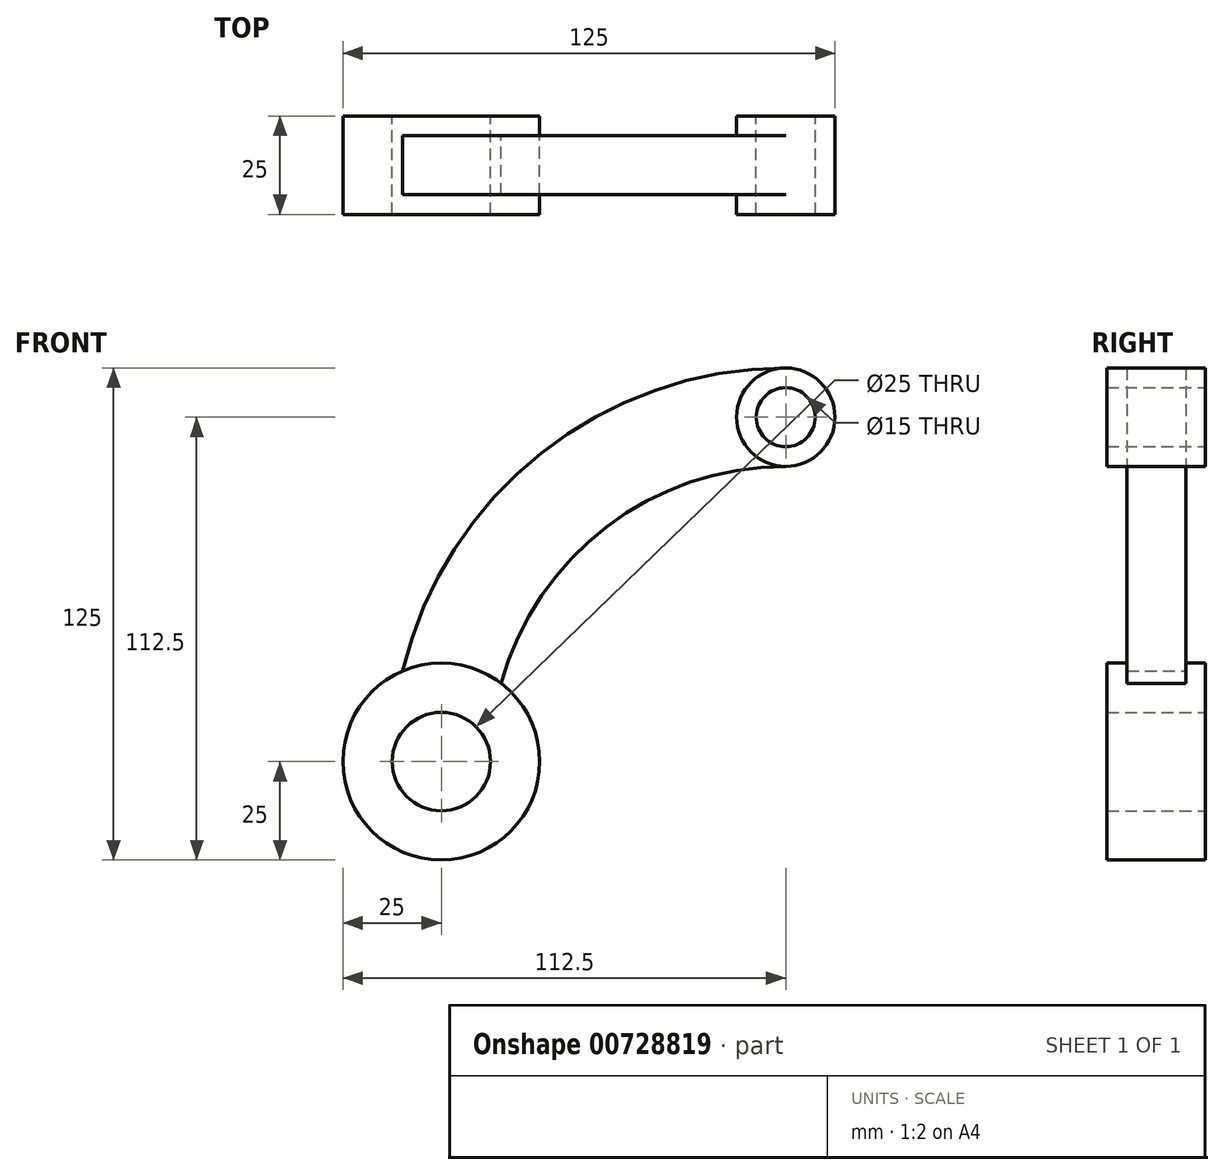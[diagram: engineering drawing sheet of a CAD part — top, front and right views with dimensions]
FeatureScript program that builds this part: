
annotation { "Feature Type Name" : "Feature", "Feature Type Description" : "" }
export const myFeature = defineFeature(function(context is Context, id is Id, definition is map)
    precondition{}
    {
        {
            var Q0;
            Q0=qCreatedBy(makeId("Front.planeOp"),FACE);
            var sketch = newSketch(context, id + "F0", { "sketchPlane" : qUnion([Q0])});
            skArc(sketch, "E0", {"start": v(0, 100) * mm, "mid": v(-62.05, 78.42) * mm, "end": v(-97.32, 22.99) * mm});
            skArc(sketch, "E1", {"start": v(0, 75) * mm, "mid": v(-45.47, 59.64) * mm, "end": v(-72.32, 19.86) * mm});
            skCircle(sketch, "E2", {"center": v(-87.5, 0) * mm, "radius": 25 * mm});
            skCircle(sketch, "E3", {"center": v(-87.5, 0) * mm, "radius": 12.5 * mm});
            skCircle(sketch, "E4", {"center": v(0, 87.5) * mm, "radius": 12.5 * mm});
            skCircle(sketch, "E5", {"center": v(0, 87.5) * mm, "radius": 7.5 * mm});
            skSolve(sketch);
        }
        {
            var Q0;
            Q0=makeQuery(id+"F0.imprint","IMPRINT",FACE,{"disambiguationData":[TD([[makeQuery(id+"F0.imprint","IMPRINT",EDGE,{"derivedFrom":sQuery(id+"F0.wireOp",EDGE,"E5")}),-1.0]])]});
            var Q1;
            Q1=makeQuery(id+"F0.imprint","IMPRINT",FACE,{"disambiguationData":[TD([[makeQuery(id+"F0.imprint","IMPRINT",EDGE,{"derivedFrom":sQuery(id+"F0.wireOp",EDGE,"E3")}),-1.0]])]});
            extrude(context, id + "F1", {"entities" : qUnion([Q0, Q1]), "endBound" : BoundingType.SYMMETRIC, "depth" : 25 * mm, "offsetDistance" : 25 * mm});
        }
        {
            var Q0;
            {var subQ0=sQuery(id+"F0.wireOp",EDGE,"E0");Q0=makeQuery(id+"F0.imprint","IMPRINT",FACE,{"disambiguationData":[TD([[makeQuery(id+"F0.imprint","IMPRINT",EDGE,{"derivedFrom":subQ0}),1.0]])]});}
            extrude(context, id + "F2", {"entities" : qUnion([Q0]), "operationType" : NewBodyOperationType.ADD, "endBound" : BoundingType.SYMMETRIC, "depth" : 15 * mm, "offsetDistance" : 25 * mm});
        }
    });
